# Revit family: Gira_0211631
name_source: partatom
category: Elektroinstallationen
revit_build: Autodesk Revit 2017 (Build: 20160225_1515(x64)
units: mm (PartAtom-declared; Revit-internal decimal feet)

## family parameters
Basisbauteil = Fläche
Beim Laden mit Abzugskörper schneiden = Nein
Bemaßung runder Anschluss = Durchmesser verwenden
Beschriftungsausrichtung beibehalten = Nein
Gemeinsam genutzt = Nein
Raumberechnungspunkt = Nein
Teiletyp = Normal

## types (1)
- Gira_0211631
    BIM = https://media.stage.bim.site
    Beschreibung = Cov.fr.1g ClX BS,Gira ClassiX cover frame,brass,1-gang,Notes :,- Each frame is unique.,- Highly-polished surface.
    Colour = Brass
    Data sheet = https://katalog.gira.de
    Degree of protection (IP) = IP20
    GTIN = 4010337097013
    HAN = 0211631
    Halogen free = Nein
    Hersteller = Gira
    Label space/information surface = Nein
    Material = Metal
    Material quality = Brass
    Mounting direction = Horizontal and vertical
    Number of units = 1
    Number of units horizontal = 1
    Number of units vertical = 1
    Productwebsite = http://katalog.gira.de
    Suitable for built-in installation = Nein
    Suitable for floor box = Nein
    Suitable for flush-mounted installation = Ja
    Suitable for wall duct = Nein
    Surface finishing = Glossy
    Surface protection = Other
    Transparent = Nein
    Type of fastening = Clamp mounting
    Typname = Cov.fr. 1-g ClassiX brass
    URL = https://www.gira.de
    Vorgabe-Ansicht = 1219 mm
    With hinged lid = Nein
    With mounting grid = Nein

## geometry (parser evidence)
native form markers: Sweep x2
no freeform markers — native parametric forms only
